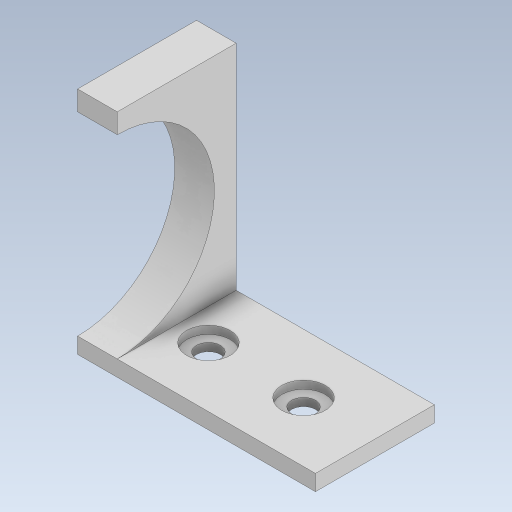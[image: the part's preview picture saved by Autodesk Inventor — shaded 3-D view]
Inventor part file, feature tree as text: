
AUTODESK INVENTOR PART (.ipt)
format: ipt  version: 2023.5 (Build 275446000, 446)  size: 323,072 bytes
history: native  units: in
note: dims shown in document units (in); Inventor stores cm internally (conversion verified against a paired STEP export)
features: extrude x5, sketch x3
ambient origin geometry x8: Origin, YZ Plane, XZ Plane, XY Plane, X Axis, Y Axis, Z Axis, Center Point
bodies: Solid1 (feature_tree)
feature tree (8):
  sketch  "Sketch1"  dims[d0=1.1811in d1=0.5906in]
  extrude  "Extrusion1"  Depth=0.5906in
  extrude  "Extrusion2"  Depth=0.0787in
  extrude  "Extrusion3"  Depth=0.2362in
  extrude  "Extrusion4"  Depth=0.0787in TaperAngle=0.0deg
  extrude  "Extrusion5"  Depth=0.0394in TaperAngle=0.0deg
  sketch  "Sketch2"  dims[d2=0.0787in d3=0.1181in]
  sketch  "Sketch3"  dims[d4=0.2165in d5=0.2362in d6=0.0787in d7=0.0in d8=0.0394in d9=0.0in d10=1.1417in d11=0.0in d13=1.1811in d14=0.0in d15=0.9646in d16=0.4823in d17=0.1181in d18=0.0in]
